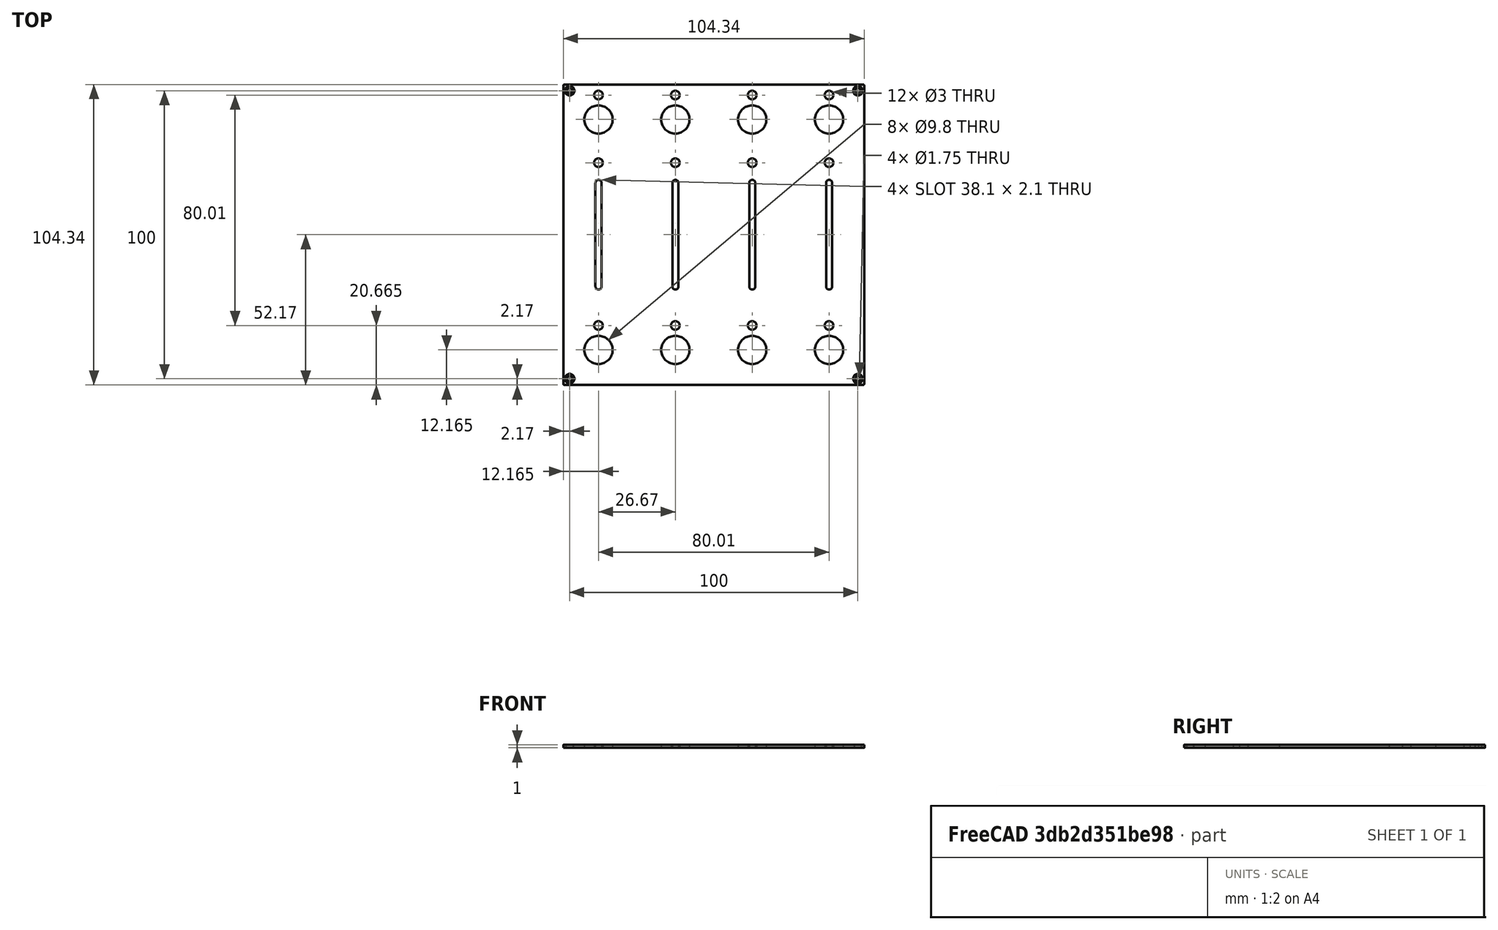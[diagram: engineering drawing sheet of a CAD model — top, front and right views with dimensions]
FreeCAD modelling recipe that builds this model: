
FCSTD DOCUMENT  (FreeCAD 0.21R33668 +26 (Git))
Label: FRONTPANEL-SHEET-PBF4
License: All rights reserved
LicenseURL: https://en.wikipedia.org/wiki/All_rights_reserved
objects: TechDraw::DrawViewBalloon×16, Sketcher::SketchObject×10, TechDraw::DrawViewDimension×9, PartDesign::Hole×6, TechDraw::DrawHatch×6, TechDraw::DrawViewPart×5, TechDraw::DrawViewAnnotation×3, TechDraw::DrawSVGTemplate×2, PartDesign::Pocket×2, PartDesign::Body×2, TechDraw::DrawPage×2, Spreadsheet::Sheet×1, PartDesign::Pad×1, PartDesign::FeatureBase×1, TechDraw::DrawComplexSection×1
note: 43 computed .brp shape members not serialized (recipe doc carries the construction recipe); baked Part::Feature solids carry a one-line shape summary decoded from their .brp

FEATURE [TechDraw::DrawSVGTemplate] Template
  EditableTexts = COLOR=Anodized matte black - RAL code: 9004; CreationDate=2024/05/14; E.G.APPROVED=APPROVED; FC-Scale=1:1; FC-Title=PBF4 - frontpanel; IntechStudioLtd.=Intech Studio Ltd.; MATERIAL=Aluminum 5052-H32; REV=04; STANDARD=ISO 2768 - m
  Height = 297
  Orientation = 1
  Template = <userpath>/Desktop/A3_LandscapeTD_MODIFIED.svg
  Width = 420
FEATURE [Spreadsheet::Sheet] Spreadsheet  label="dim"
  cells = A1='panel_length; B1(panel_length)=104.35; A2='panel_thickness; B2(panel_thickness)=1; A3='panel_radius; B3(panel_radius)==(104.35 - 103.6) / 2; A5='corner_drill_dist; B5(corner_drill_dist)=100; A6='corner_drill_dia; B6(corner_drill_dia)=1.75; A7='corner_drill_countersink; B7(corner_drill_countersink)=3.3; A9='undercut_width; B9(undercut_width)=1; A10='undercut_length; B10(undercut_length)=90; A11='undercut_offset; B11(undercut_offset)=1; A12='undercut_depth; B12(undercut_depth)=0.8; A14='ui_raster; B14(ui_raster)=26.67; A16='light_drill_dia; B16(light_drill_dia)=3; D16='old 2.9; A17='light_bore_dia; B17(light_bore_dia)=3.45; C17='check; D17='old 3.30; E17='DEPRICATED; A18='light_bore_depth; B18(light_bore_depth)=0.4; C18='check; D18='old 0.40; E18='DEPRICATED; A20='pot_drill_dia; B20(pot_drill_dia)=9.8; C20='check; D20='old 6.20; A21='pot_led_dist; B21(pot_led_dist)=8.5; B22=0; A23='but_drill_dia; B23(but_drill_dia)=9.8; A24='but_led_dist; B24(but_led_dist)=8.5; A26='fad_cutout_width; B26(fad_cutout_width)=2.1; C26='check; D26='old 1.50; A27='fad_cutout_length; B27(fad_cutout_length)=36; A28='fad_led_dist; B28(fad_led_dist)=25; A30='enc_drill_dia; B30(enc_drill_dia)=9.8; C30='check; D30='old 6.20; A31='enc_led_dist; B31(enc_led_dist)=8.5; A33='longfad_cutout_width; B33(longfad_cutout_width)=2.1; A34='longfad_cutout_length; B34(longfad_cutout_length)=66; A36='panel_chamfer; B36(panel_chamfer)=0.2; C36='UPDATE DRAWING
FEATURE [Sketcher::SketchObject] Sketch012
  FullyConstrained = true
  MapMode = 5
  Support = -> [XY_Plane003]
  expr: Constraints[21] = <<dim>>.fad_led_dist
  expr: Constraints[4] = <<dim>>.ui_raster
  sketch-geometry (9):
    g0: Circle CenterX=-40.005 CenterY=25 CenterZ=0 NormalX=0 NormalY=0 NormalZ=1 AngleXU=0 Radius=2
    g1: Circle CenterX=-13.335 CenterY=25 CenterZ=0 NormalX=0 NormalY=0 NormalZ=1 AngleXU=0 Radius=2
    g2: LineSegment StartX=-40.005 StartY=25 StartZ=0 EndX=-13.335 EndY=25 EndZ=0
    g3: Circle CenterX=13.335 CenterY=25 CenterZ=0 NormalX=0 NormalY=0 NormalZ=1 AngleXU=0 Radius=2
    g4: LineSegment StartX=-13.335 StartY=25 StartZ=0 EndX=13.335 EndY=25 EndZ=0
    g5: Circle CenterX=40.005 CenterY=25 CenterZ=0 NormalX=0 NormalY=0 NormalZ=1 AngleXU=0 Radius=2
    g6: LineSegment StartX=13.335 StartY=25 StartZ=0 EndX=40.005 EndY=25 EndZ=0
    g7: LineSegment StartX=-13.335 StartY=25 StartZ=0 EndX=0 EndY=0 EndZ=0
    g8: LineSegment StartX=0 StartY=0 StartZ=0 EndX=13.335 EndY=25 EndZ=0
  constraints (22):
    c: Diameter(g0) = 4
    c: Diameter(g1) = 4
    c: Coincident(g0,g2)
    c: Coincident(g1,g2)
    c: Distance(g2) = 26.67
    c: Angle(g2) = 0
    c: Diameter(g3) = 4
    c: Coincident(g1,g4)
    c: Coincident(g3,g4)
    c: Equal(g2,g4)
    c: Parallel(g4,g2)
    c: Diameter(g5) = 4
    c: Coincident(g3,g6)
    c: Coincident(g5,g6)
    c: Equal(g2,g6)
    c: Parallel(g6,g2)
    c: Coincident(g7,g1)
    c: Coincident(g7,g-1)
    c: Coincident(g7,g8)
    c: Coincident(g8,g3)
    c: Equal(g8,g7)
    c: DistanceY(g-1,g0) = 25
FEATURE [Sketcher::SketchObject] Sketch011
  FullyConstrained = true
  MapMode = 5
  Support = -> [XY_Plane003]
  expr: Constraints[17] = <<dim>>.ui_raster
  expr: Constraints[6] = <<dim>>.fad_cutout_width
  expr: Constraints[7] = <<dim>>.fad_cutout_length
  sketch-geometry (22):
    g0: ArcOfCircle CenterX=-40.005 CenterY=18 CenterZ=0 NormalX=0 NormalY=0 NormalZ=1 AngleXU=0 Radius=1.05 StartAngle=-1.26832e-11 EndAngle=3.14159
    g1: ArcOfCircle CenterX=-40.005 CenterY=-18 CenterZ=0 NormalX=0 NormalY=0 NormalZ=1 AngleXU=0 Radius=1.05 StartAngle=3.14159 EndAngle=6.28319
    g2: LineSegment StartX=-41.055 StartY=18 StartZ=0 EndX=-41.055 EndY=-18 EndZ=0
    g3: LineSegment StartX=-38.955 StartY=18 StartZ=0 EndX=-38.955 EndY=-18 EndZ=0
    g4: ArcOfCircle CenterX=-13.335 CenterY=18 CenterZ=0 NormalX=0 NormalY=0 NormalZ=1 AngleXU=0 Radius=1.05 StartAngle=2e-16 EndAngle=3.14159
    g5: ArcOfCircle CenterX=-13.335 CenterY=-18 CenterZ=0 NormalX=0 NormalY=0 NormalZ=1 AngleXU=0 Radius=1.05 StartAngle=3.14159 EndAngle=6.28319
    g6: LineSegment StartX=-14.385 StartY=18 StartZ=0 EndX=-14.385 EndY=-18 EndZ=0
    g7: LineSegment StartX=-12.285 StartY=18 StartZ=0 EndX=-12.285 EndY=-18 EndZ=0
    g8: LineSegment StartX=-38.955 StartY=18 StartZ=0 EndX=-12.285 EndY=18 EndZ=0
    g9: ArcOfCircle CenterX=13.335 CenterY=18 CenterZ=0 NormalX=0 NormalY=0 NormalZ=1 AngleXU=0 Radius=1.05 StartAngle=1.1e-15 EndAngle=3.14159
    g10: ArcOfCircle CenterX=13.335 CenterY=-18 CenterZ=0 NormalX=0 NormalY=0 NormalZ=1 AngleXU=0 Radius=1.05 StartAngle=3.14159 EndAngle=6.28319
    g11: LineSegment StartX=12.285 StartY=18 StartZ=0 EndX=12.285 EndY=-18 EndZ=0
    g12: LineSegment StartX=14.385 StartY=18 StartZ=0 EndX=14.385 EndY=-18 EndZ=0
    g13: LineSegment StartX=-12.285 StartY=18 StartZ=0 EndX=14.385 EndY=18 EndZ=0
    g14: ArcOfCircle CenterX=40.005 CenterY=18 CenterZ=0 NormalX=0 NormalY=0 NormalZ=1 AngleXU=0 Radius=1.05 StartAngle=9e-16 EndAngle=3.14159
    g15: ArcOfCircle CenterX=40.005 CenterY=-18 CenterZ=0 NormalX=0 NormalY=0 NormalZ=1 AngleXU=0 Radius=1.05 StartAngle=3.14159 EndAngle=6.28319
    g16: LineSegment StartX=38.955 StartY=18 StartZ=0 EndX=38.955 EndY=-18 EndZ=0
    g17: LineSegment StartX=41.055 StartY=18 StartZ=0 EndX=41.055 EndY=-18 EndZ=0
    g18: LineSegment StartX=14.385 StartY=18 StartZ=0 EndX=41.055 EndY=18 EndZ=0
    g19: LineSegment StartX=-13.335 StartY=18 StartZ=0 EndX=0 EndY=0 EndZ=0
    g20: LineSegment StartX=0 StartY=0 StartZ=0 EndX=13.335 EndY=18 EndZ=0
    g21: LineSegment StartX=0 StartY=0 StartZ=0 EndX=-13.335 EndY=-18 EndZ=0
  constraints (52):
    c: Tangent(g0,g3) = 1.5708
    c: Tangent(g0,g2) = -1.5708
    c: Tangent(g2,g1) = -1.5708
    c: Tangent(g3,g1) = 1.5708
    c: Vertical(g2)
    c: Equal(g0,g1)
    c: DistanceX(g0,g0) = 2.1
    c: DistanceY(g1,g0) = 36
    c: Tangent(g4,g7) = 1.5708
    c: Tangent(g4,g6) = -1.5708
    c: Tangent(g6,g5) = -1.5708
    c: Tangent(g7,g5) = 1.5708
    c: Vertical(g6)
    c: Equal(g4,g5)
    c: DistanceY(g5,g4) = 36
    c: Coincident(g0,g8)
    c: Coincident(g4,g8)
    c: Distance(g8) = 26.67
    c: Angle(g8) = 0
    c: Tangent(g9,g12) = 1.5708
    c: Tangent(g9,g11) = -1.5708
    c: Tangent(g11,g10) = -1.5708
    c: Tangent(g12,g10) = 1.5708
    c: Vertical(g11)
    c: Equal(g9,g10)
    c: DistanceY(g10,g9) = 36
    c: Coincident(g4,g13)
    c: Coincident(g9,g13)
    c: Equal(g8,g13)
    c: Parallel(g13,g8)
    c: Tangent(g14,g17) = 1.5708
    c: Tangent(g14,g16) = -1.5708
    c: Tangent(g16,g15) = -1.5708
    c: Tangent(g17,g15) = 1.5708
    c: Vertical(g16)
    c: Equal(g14,g15)
    c: DistanceY(g15,g14) = 36
    c: Coincident(g9,g18)
    c: Coincident(g14,g18)
    c: Equal(g8,g18)
    c: Parallel(g18,g8)
    c: Coincident(g19,g4)
    c: Coincident(g19,g-1)
    c: Coincident(g19,g20)
    c: Coincident(g20,g9)
    c: Coincident(g-1,g21)
    c: Coincident(g21,g5)
    c: Equal(g21,g19)
    c: Equal(g19,g20)
    c: Equal(g4,g9)
    c: Equal(g9,g14)
    c: Equal(g14,g0)
FEATURE [Sketcher::SketchObject] Sketch010
  FullyConstrained = true
  MapMode = 5
  Support = -> [XY_Plane003]
  expr: Constraints[20] = <<dim>>.ui_raster * 1.5
  expr: Constraints[21] = <<dim>>.pot_led_dist
  expr: Constraints[4] = <<dim>>.ui_raster
  sketch-geometry (9):
    g0: Circle CenterX=-40.005 CenterY=48.505 CenterZ=0 NormalX=0 NormalY=0 NormalZ=1 AngleXU=0 Radius=2
    g1: Circle CenterX=-13.335 CenterY=48.505 CenterZ=0 NormalX=0 NormalY=0 NormalZ=1 AngleXU=0 Radius=2
    g2: LineSegment StartX=-40.005 StartY=48.505 StartZ=0 EndX=-13.335 EndY=48.505 EndZ=0
    g3: Circle CenterX=13.335 CenterY=48.505 CenterZ=0 NormalX=0 NormalY=0 NormalZ=1 AngleXU=0 Radius=2
    g4: LineSegment StartX=-13.335 StartY=48.505 StartZ=0 EndX=13.335 EndY=48.505 EndZ=0
    g5: Circle CenterX=40.005 CenterY=48.505 CenterZ=0 NormalX=0 NormalY=0 NormalZ=1 AngleXU=0 Radius=2
    g6: LineSegment StartX=13.335 StartY=48.505 StartZ=0 EndX=40.005 EndY=48.505 EndZ=0
    g7: LineSegment StartX=-13.335 StartY=48.505 StartZ=0 EndX=0 EndY=40.005 EndZ=0
    g8: LineSegment StartX=0 StartY=40.005 StartZ=0 EndX=13.335 EndY=48.505 EndZ=0
  constraints (23):
    c: Diameter(g0) = 4
    c: Diameter(g1) = 4
    c: Coincident(g0,g2)
    c: Coincident(g1,g2)
    c: Distance(g2) = 26.67
    c: Angle(g2) = 0
    c: Diameter(g3) = 4
    c: Coincident(g1,g4)
    c: Coincident(g3,g4)
    c: Equal(g2,g4)
    c: Parallel(g4,g2)
    c: Diameter(g5) = 4
    c: Coincident(g3,g6)
    c: Coincident(g5,g6)
    c: Equal(g2,g6)
    c: Parallel(g6,g2)
    c: Coincident(g7,g1)
    c: PointOnObject(g7,g-2)
    c: Coincident(g7,g8)
    c: Coincident(g8,g3)
    c: DistanceY(g-1,g7) = 40.005
    c: DistanceY(g7,g1) = 8.5
    c: Equal(g8,g7)
FEATURE [Sketcher::SketchObject] Sketch009
  FullyConstrained = true
  MapMode = 5
  Support = -> [XY_Plane003]
  expr: Constraints[21] = <<dim>>.ui_raster * 1.5
  expr: Constraints[4] = <<dim>>.ui_raster
  sketch-geometry (9):
    g0: Circle CenterX=-40.005 CenterY=40.005 CenterZ=0 NormalX=0 NormalY=0 NormalZ=1 AngleXU=0 Radius=2
    g1: Circle CenterX=-13.335 CenterY=40.005 CenterZ=0 NormalX=0 NormalY=0 NormalZ=1 AngleXU=0 Radius=2
    g2: LineSegment StartX=-40.005 StartY=40.005 StartZ=0 EndX=-13.335 EndY=40.005 EndZ=0
    g3: Circle CenterX=13.335 CenterY=40.005 CenterZ=0 NormalX=0 NormalY=0 NormalZ=1 AngleXU=0 Radius=2
    g4: LineSegment StartX=-13.335 StartY=40.005 StartZ=0 EndX=13.335 EndY=40.005 EndZ=0
    g5: Circle CenterX=40.005 CenterY=40.005 CenterZ=0 NormalX=0 NormalY=0 NormalZ=1 AngleXU=0 Radius=2
    g6: LineSegment StartX=13.335 StartY=40.005 StartZ=0 EndX=40.005 EndY=40.005 EndZ=0
    g7: LineSegment StartX=-13.335 StartY=40.005 StartZ=0 EndX=0 EndY=0 EndZ=0
    g8: LineSegment StartX=0 StartY=0 StartZ=0 EndX=13.335 EndY=40.005 EndZ=0
  constraints (22):
    c: Diameter(g0) = 4
    c: Diameter(g1) = 4
    c: Coincident(g0,g2)
    c: Coincident(g1,g2)
    c: Distance(g2) = 26.67
    c: Angle(g2) = 0
    c: Diameter(g3) = 4
    c: Coincident(g1,g4)
    c: Coincident(g3,g4)
    c: Equal(g2,g4)
    c: Parallel(g4,g2)
    c: Diameter(g5) = 4
    c: Coincident(g3,g6)
    c: Coincident(g5,g6)
    c: Equal(g2,g6)
    c: Parallel(g6,g2)
    c: Coincident(g7,g1)
    c: Coincident(g7,g-1)
    c: Coincident(g7,g8)
    c: Coincident(g8,g3)
    c: Equal(g7,g8)
    c: DistanceY(g-1,g0) = 40.005
FEATURE [Sketcher::SketchObject] Sketch008
  FullyConstrained = true
  MapMode = 5
  Support = -> [XY_Plane003]
  expr: Constraints[21] = <<dim>>.ui_raster * 1.5
  expr: Constraints[22] = <<dim>>.but_led_dist
  expr: Constraints[4] = <<dim>>.ui_raster
  sketch-geometry (9):
    g0: Circle CenterX=-40.005 CenterY=-31.505 CenterZ=0 NormalX=0 NormalY=0 NormalZ=1 AngleXU=0 Radius=2
    g1: Circle CenterX=-13.335 CenterY=-31.505 CenterZ=0 NormalX=0 NormalY=0 NormalZ=1 AngleXU=0 Radius=2
    g2: LineSegment StartX=-40.005 StartY=-31.505 StartZ=0 EndX=-13.335 EndY=-31.505 EndZ=0
    g3: Circle CenterX=13.335 CenterY=-31.505 CenterZ=0 NormalX=0 NormalY=0 NormalZ=1 AngleXU=0 Radius=2
    g4: LineSegment StartX=-13.335 StartY=-31.505 StartZ=0 EndX=13.335 EndY=-31.505 EndZ=0
    g5: Circle CenterX=40.005 CenterY=-31.505 CenterZ=0 NormalX=0 NormalY=0 NormalZ=1 AngleXU=0 Radius=2
    g6: LineSegment StartX=13.335 StartY=-31.505 StartZ=0 EndX=40.005 EndY=-31.505 EndZ=0
    g7: LineSegment StartX=-13.335 StartY=-31.505 StartZ=0 EndX=0 EndY=-40.005 EndZ=0
    g8: LineSegment StartX=0 StartY=-40.005 StartZ=0 EndX=13.335 EndY=-31.505 EndZ=0
  constraints (23):
    c: Diameter(g0) = 4
    c: Diameter(g1) = 4
    c: Coincident(g0,g2)
    c: Coincident(g1,g2)
    c: Distance(g2) = 26.67
    c: Angle(g2) = 0
    c: Diameter(g3) = 4
    c: Coincident(g1,g4)
    c: Coincident(g3,g4)
    c: Equal(g2,g4)
    c: Parallel(g4,g2)
    c: Diameter(g5) = 4
    c: Coincident(g3,g6)
    c: Coincident(g5,g6)
    c: Equal(g2,g6)
    c: Parallel(g6,g2)
    c: Coincident(g7,g1)
    c: PointOnObject(g7,g-2)
    c: Coincident(g8,g7)
    c: Coincident(g8,g3)
    c: Equal(g8,g7)
    c: DistanceY(g7,g-1) = 40.005
    c: DistanceY(g7,g0) = 8.5
FEATURE [Sketcher::SketchObject] Sketch007
  FullyConstrained = true
  MapMode = 5
  Support = -> [XY_Plane003]
  expr: Constraints[16] = <<dim>>.ui_raster * 1.5
  expr: Constraints[4] = <<dim>>.ui_raster
  sketch-geometry (9):
    g0: Circle CenterX=-40.005 CenterY=-40.005 CenterZ=0 NormalX=0 NormalY=0 NormalZ=1 AngleXU=0 Radius=2
    g1: Circle CenterX=-13.335 CenterY=-40.005 CenterZ=0 NormalX=0 NormalY=0 NormalZ=1 AngleXU=0 Radius=2
    g2: LineSegment StartX=-40.005 StartY=-40.005 StartZ=0 EndX=-13.335 EndY=-40.005 EndZ=0
    g3: Circle CenterX=13.335 CenterY=-40.005 CenterZ=0 NormalX=0 NormalY=0 NormalZ=1 AngleXU=0 Radius=2
    g4: LineSegment StartX=-13.335 StartY=-40.005 StartZ=0 EndX=13.335 EndY=-40.005 EndZ=0
    g5: Circle CenterX=40.005 CenterY=-40.005 CenterZ=0 NormalX=0 NormalY=0 NormalZ=1 AngleXU=0 Radius=2
    g6: LineSegment StartX=13.335 StartY=-40.005 StartZ=0 EndX=40.005 EndY=-40.005 EndZ=0
    g7: LineSegment StartX=-13.335 StartY=-40.005 StartZ=0 EndX=0 EndY=0 EndZ=0
    g8: LineSegment StartX=0 StartY=0 StartZ=0 EndX=13.335 EndY=-40.005 EndZ=0
  constraints (22):
    c: Diameter(g0) = 4
    c: Diameter(g1) = 4
    c: Coincident(g0,g2)
    c: Coincident(g1,g2)
    c: Distance(g2) = 26.67
    c: Angle(g2) = 0
    c: Diameter(g3) = 4
    c: Coincident(g1,g4)
    c: Coincident(g3,g4)
    c: Equal(g2,g4)
    c: Parallel(g4,g2)
    c: Diameter(g5) = 4
    c: Coincident(g3,g6)
    c: Coincident(g5,g6)
    c: Equal(g2,g6)
    c: Parallel(g6,g2)
    c: DistanceY(g0,g-1) = 40.005
    c: Coincident(g7,g1)
    c: Coincident(g7,g-1)
    c: Coincident(g7,g8)
    c: Coincident(g8,g3)
    c: Equal(g8,g7)
FEATURE [Sketcher::SketchObject] Sketch001
  FullyConstrained = true
  MapMode = 5
  Support = -> [XY_Plane]
  expr: Constraints[13] = <<dim>>.corner_drill_dist
  sketch-geometry (9):
    g0: LineSegment StartX=-50 StartY=50 StartZ=0 EndX=-50 EndY=-50 EndZ=0
    g1: LineSegment StartX=-50 StartY=-50 StartZ=0 EndX=50 EndY=-50 EndZ=0
    g2: LineSegment StartX=50 StartY=-50 StartZ=0 EndX=50 EndY=50 EndZ=0
    g3: LineSegment StartX=50 StartY=50 StartZ=0 EndX=-50 EndY=50 EndZ=0
    g4: Circle CenterX=0 CenterY=0 CenterZ=0 NormalX=0 NormalY=0 NormalZ=1 AngleXU=0 Radius=70.7107
    g5: Circle CenterX=-50 CenterY=50 CenterZ=0 NormalX=0 NormalY=0 NormalZ=1 AngleXU=0 Radius=0.5
    g6: Circle CenterX=50 CenterY=50 CenterZ=0 NormalX=0 NormalY=0 NormalZ=1 AngleXU=0 Radius=0.5
    g7: Circle CenterX=50 CenterY=-50 CenterZ=0 NormalX=0 NormalY=0 NormalZ=1 AngleXU=0 Radius=0.5
    g8: Circle CenterX=-50 CenterY=-50 CenterZ=0 NormalX=0 NormalY=0 NormalZ=1 AngleXU=0 Radius=0.5
  constraints (22):
    c: Coincident(g0,g1)
    c: Coincident(g1,g2)
    c: Coincident(g2,g3)
    c: Coincident(g3,g0)
    c: Equal(g0,g1)
    c: Equal(g0,g2)
    c: Equal(g0,g3)
    c: PointOnObject(g0,g4)
    c: PointOnObject(g1,g4)
    c: PointOnObject(g2,g4)
    c: PointOnObject(g3,g4)
    c: Coincident(g4,g-1)
    c: Horizontal(g3)
    c: DistanceX(g3,g3) = 100
    c: Coincident(g5,g0)
    c: Coincident(g6,g2)
    c: Coincident(g7,g1)
    c: Coincident(g8,g0)
    c: Diameter(g8) = 1
    c: Equal(g8,g7)
    c: Equal(g8,g6)
    c: Equal(g8,g5)
FEATURE [Sketcher::SketchObject] Sketch002
  AttachmentOffset = pos=(0,0,-4.8) rot=(0,0,1;0rad)
  FullyConstrained = true
  MapMode = 5
  Placement = pos=(0,0,-4.8) rot=(0,0,1;0rad)
  Support = -> [XY_Plane]
  expr: .AttachmentOffset.Base.z = -<<dim>>.undercut_depth - 4
  expr: Constraints[91] = <<dim>>.undercut_length
  expr: Constraints[92] = <<dim>>.undercut_width
  expr: Constraints[93] = <<dim>>.panel_length / 2 - <<dim>>.undercut_offset - <<dim>>.undercut_width / 2
  sketch-geometry (40):
    g0: LineSegment StartX=-45 StartY=50.175 StartZ=0 EndX=45 EndY=50.175 EndZ=0
    g1: LineSegment StartX=-45 StartY=51.175 StartZ=0 EndX=45 EndY=51.175 EndZ=0
    g2: LineSegment StartX=-50.675 StartY=45 StartZ=0 EndX=0 EndY=0 EndZ=0
    g3: LineSegment StartX=0 StartY=0 StartZ=0 EndX=-50.675 EndY=-45 EndZ=0
    g4: LineSegment StartX=0 StartY=0 StartZ=0 EndX=-45 EndY=50.675 EndZ=0
    g5: LineSegment StartX=45 StartY=50.675 StartZ=0 EndX=0 EndY=0 EndZ=0
    g6: LineSegment StartX=0 StartY=0 StartZ=0 EndX=50.675 EndY=45 EndZ=0
    g7: LineSegment StartX=50.675 StartY=-45 StartZ=0 EndX=0 EndY=0 EndZ=0
    g8: LineSegment StartX=0 StartY=0 StartZ=0 EndX=45 EndY=-50.675 EndZ=0
    g9: LineSegment StartX=0 StartY=0 StartZ=0 EndX=-45 EndY=-50.675 EndZ=0
    g10: ArcOfCircle CenterX=45 CenterY=50.675 CenterZ=0 NormalX=0 NormalY=0 NormalZ=1 AngleXU=0 Radius=0.5 StartAngle=4.71239 EndAngle=6.28319
    g11: ArcOfCircle CenterX=45 CenterY=50.675 CenterZ=0 NormalX=0 NormalY=0 NormalZ=1 AngleXU=0 Radius=0.5 StartAngle=0 EndAngle=1.5708
    g12: LineSegment StartX=45 StartY=50.675 StartZ=0 EndX=45.5 EndY=50.675 EndZ=0
    g13: ArcOfCircle CenterX=-45 CenterY=50.675 CenterZ=0 NormalX=0 NormalY=0 NormalZ=1 AngleXU=0 Radius=0.5 StartAngle=3.14159 EndAngle=4.71239
    g14: ArcOfCircle CenterX=-45 CenterY=50.675 CenterZ=0 NormalX=0 NormalY=0 NormalZ=1 AngleXU=0 Radius=0.5 StartAngle=1.5708 EndAngle=3.14159
    g15: LineSegment StartX=-45.5 StartY=50.675 StartZ=0 EndX=-45 EndY=50.675 EndZ=0
    g16: LineSegment StartX=-45 StartY=-51.175 StartZ=0 EndX=45 EndY=-51.175 EndZ=0
    g17: LineSegment StartX=-45 StartY=-50.175 StartZ=0 EndX=45 EndY=-50.175 EndZ=0
    g18: ArcOfCircle CenterX=45 CenterY=-50.675 CenterZ=0 NormalX=0 NormalY=0 NormalZ=1 AngleXU=0 Radius=0.5 StartAngle=4.71239 EndAngle=6.28319
    g19: ArcOfCircle CenterX=45 CenterY=-50.675 CenterZ=0 NormalX=0 NormalY=0 NormalZ=1 AngleXU=0 Radius=0.5 StartAngle=0 EndAngle=1.5708
    g20: LineSegment StartX=45 StartY=-50.675 StartZ=0 EndX=45.5 EndY=-50.675 EndZ=0
    g21: ArcOfCircle CenterX=-45 CenterY=-50.675 CenterZ=0 NormalX=0 NormalY=0 NormalZ=1 AngleXU=0 Radius=0.5 StartAngle=3.14159 EndAngle=4.71239
    g22: ArcOfCircle CenterX=-45 CenterY=-50.675 CenterZ=0 NormalX=0 NormalY=0 NormalZ=1 AngleXU=0 Radius=0.5 StartAngle=1.5708 EndAngle=3.14159
    g23: LineSegment StartX=-45.5 StartY=-50.675 StartZ=0 EndX=-45 EndY=-50.675 EndZ=0
    g24: LineSegment StartX=51.175 StartY=-45 StartZ=0 EndX=51.175 EndY=45 EndZ=0
    g25: LineSegment StartX=50.175 StartY=-45 StartZ=0 EndX=50.175 EndY=45 EndZ=0
    g26: ArcOfCircle CenterX=50.675 CenterY=45 CenterZ=0 NormalX=0 NormalY=0 NormalZ=1 AngleXU=0 Radius=0.5 StartAngle=3.8e-15 EndAngle=1.5708
    g27: ArcOfCircle CenterX=50.675 CenterY=45 CenterZ=0 NormalX=0 NormalY=0 NormalZ=1 AngleXU=0 Radius=0.5 StartAngle=1.5708 EndAngle=3.14159
    g28: LineSegment StartX=50.675 StartY=45 StartZ=0 EndX=50.675 EndY=45.5 EndZ=0
    g29: ArcOfCircle CenterX=50.675 CenterY=-45 CenterZ=0 NormalX=0 NormalY=0 NormalZ=1 AngleXU=0 Radius=0.5 StartAngle=4.71239 EndAngle=6.28319
    g30: ArcOfCircle CenterX=50.675 CenterY=-45 CenterZ=0 NormalX=0 NormalY=0 NormalZ=1 AngleXU=0 Radius=0.5 StartAngle=3.14159 EndAngle=4.71239
    g31: LineSegment StartX=50.675 StartY=-45.5 StartZ=0 EndX=50.675 EndY=-45 EndZ=0
    g32: LineSegment StartX=-50.175 StartY=-45 StartZ=0 EndX=-50.175 EndY=45 EndZ=0
    g33: LineSegment StartX=-51.175 StartY=-45 StartZ=0 EndX=-51.175 EndY=45 EndZ=0
    g34: ArcOfCircle CenterX=-50.675 CenterY=45 CenterZ=0 NormalX=0 NormalY=0 NormalZ=1 AngleXU=0 Radius=0.5 StartAngle=1.4e-15 EndAngle=1.5708
    g35: ArcOfCircle CenterX=-50.675 CenterY=45 CenterZ=0 NormalX=0 NormalY=0 NormalZ=1 AngleXU=0 Radius=0.5 StartAngle=1.5708 EndAngle=3.14159
    g36: LineSegment StartX=-50.675 StartY=45 StartZ=0 EndX=-50.675 EndY=45.5 EndZ=0
    g37: ArcOfCircle CenterX=-50.675 CenterY=-45 CenterZ=0 NormalX=0 NormalY=0 NormalZ=1 AngleXU=0 Radius=0.5 StartAngle=4.71239 EndAngle=6.28319
    g38: ArcOfCircle CenterX=-50.675 CenterY=-45 CenterZ=0 NormalX=0 NormalY=0 NormalZ=1 AngleXU=0 Radius=0.5 StartAngle=3.14159 EndAngle=4.71239
    g39: LineSegment StartX=-50.675 StartY=-45.5 StartZ=0 EndX=-50.675 EndY=-45 EndZ=0
  constraints (96):
    c: Horizontal(g0)
    c: Coincident(g2,g-1)
    c: Coincident(g2,g3)
    c: Coincident(g-1,g4)
    c: Coincident(g5,g-1)
    c: Coincident(g5,g6)
    c: Coincident(g7,g-1)
    c: Coincident(g7,g8)
    c: Coincident(g-1,g9)
    c: Equal(g5,g6)
    c: Equal(g6,g8)
    c: Equal(g8,g7)
    c: Equal(g7,g9)
    c: Equal(g9,g3)
    c: Equal(g3,g2)
    c: Equal(g2,g4)
    c: Coincident(g10,g5)
    c: Coincident(g11,g10)
    c: Coincident(g11,g10)
    c: Tangent(g11,g1) = 1.5708
    c: Tangent(g10,g0) = -1.5708
    c: Coincident(g12,g10)
    c: Coincident(g12,g10)
    c: Horizontal(g12)
    c: Coincident(g13,g4)
    c: Coincident(g14,g13)
    c: Coincident(g14,g13)
    c: Tangent(g14,g1) = 1.5708
    c: Tangent(g13,g0) = -1.5708
    c: Coincident(g15,g13)
    c: Coincident(g15,g13)
    c: Horizontal(g15)
    c: Horizontal(g1)
    c: Horizontal(g16)
    c: Coincident(g19,g18)
    c: Coincident(g19,g18)
    c: Tangent(g19,g17) = 1.5708
    c: Tangent(g18,g16) = -1.5708
    c: Coincident(g20,g18)
    c: Coincident(g20,g18)
    c: Horizontal(g20)
    c: Coincident(g22,g21)
    c: Coincident(g22,g21)
    c: Tangent(g22,g17) = 1.5708
    c: Tangent(g21,g16) = -1.5708
    c: Coincident(g23,g21)
    c: Coincident(g23,g21)
    c: Horizontal(g23)
    c: Horizontal(g17)
    c: Coincident(g21,g9)
    c: Coincident(g8,g18)
    c: Equal(g22,g14)
    c: Equal(g17,g1)
    c: Coincident(g27,g26)
    c: Coincident(g27,g26)
    c: Tangent(g27,g25) = 1.5708
    c: Tangent(g26,g24) = -1.5708
    c: Coincident(g28,g26)
    c: Coincident(g28,g26)
    c: Coincident(g30,g29)
    c: Coincident(g30,g29)
    c: Tangent(g30,g25) = 1.5708
    c: Tangent(g29,g24) = -1.5708
    c: Coincident(g31,g29)
    c: Coincident(g31,g29)
    c: Vertical(g31)
    c: Vertical(g28)
    c: Vertical(g25)
    c: Vertical(g24)
    c: Coincident(g35,g34)
    c: Coincident(g35,g34)
    c: Tangent(g35,g33) = 1.5708
    c: Tangent(g34,g32) = -1.5708
    c: Coincident(g36,g34)
    c: Coincident(g36,g34)
    c: Coincident(g38,g37)
    c: Coincident(g38,g37)
    c: Tangent(g38,g33) = 1.5708
    c: Tangent(g37,g32) = -1.5708
    c: Coincident(g39,g37)
    c: Coincident(g39,g37)
    c: Vertical(g39)
    c: Vertical(g36)
    c: Vertical(g33)
    c: Vertical(g32)
    c: Coincident(g6,g26)
    c: Coincident(g7,g29)
    c: Equal(g25,g0)
    c: Equal(g11,g27)
    c: Equal(g1,g33)
    c: Equal(g35,g11)
    c: DistanceX(g13,g10) = 90
    c: Diameter(g13) = 1
    c: DistanceY(g-1,g13) = 50.675
    c: Coincident(g2,g34)
    c: Coincident(g3,g37)
FEATURE [Sketcher::SketchObject] Sketch
  FullyConstrained = true
  MapMode = 5
  Support = -> [XY_Plane]
  expr: Constraints[12] = <<dim>>.panel_radius
  expr: Constraints[16] = <<dim>>.panel_length
  sketch-geometry (11):
    g0: LineSegment StartX=-51.8 StartY=52.175 StartZ=0 EndX=51.8 EndY=52.175 EndZ=0
    g1: LineSegment StartX=52.175 StartY=51.8 StartZ=0 EndX=52.175 EndY=-51.8 EndZ=0
    g2: LineSegment StartX=51.8 StartY=-52.175 StartZ=0 EndX=-51.8 EndY=-52.175 EndZ=0
    g3: LineSegment StartX=-52.175 StartY=-51.8 StartZ=0 EndX=-52.175 EndY=51.8 EndZ=0
    g4: ArcOfCircle CenterX=-51.8 CenterY=51.8 CenterZ=0 NormalX=0 NormalY=0 NormalZ=1 AngleXU=0 Radius=0.375 StartAngle=1.5708 EndAngle=3.14159
    g5: ArcOfCircle CenterX=51.8 CenterY=51.8 CenterZ=0 NormalX=0 NormalY=0 NormalZ=1 AngleXU=0 Radius=0.375 StartAngle=8.4e-15 EndAngle=1.5708
    g6: ArcOfCircle CenterX=51.8 CenterY=-51.8 CenterZ=0 NormalX=0 NormalY=0 NormalZ=1 AngleXU=0 Radius=0.375 StartAngle=4.71239 EndAngle=6.28319
    g7: ArcOfCircle CenterX=-51.8 CenterY=-51.8 CenterZ=0 NormalX=0 NormalY=0 NormalZ=1 AngleXU=0 Radius=0.375 StartAngle=3.14159 EndAngle=4.71239
    g8: LineSegment StartX=-51.8 StartY=51.8 StartZ=0 EndX=0 EndY=0 EndZ=0
    g9: LineSegment StartX=0 StartY=0 StartZ=0 EndX=51.8 EndY=51.8 EndZ=0
    g10: LineSegment StartX=0 StartY=0 StartZ=0 EndX=-51.8 EndY=-51.8 EndZ=0
  constraints (26):
    c: Horizontal(g0)
    c: Horizontal(g2)
    c: Vertical(g1)
    c: Vertical(g3)
    c: Tangent(g3,g4) = 1.5708
    c: Tangent(g0,g4) = 1.5708
    c: Tangent(g0,g5) = 1.5708
    c: Tangent(g1,g5) = 1.5708
    c: Tangent(g1,g6) = 1.5708
    c: Tangent(g2,g6) = 1.5708
    c: Tangent(g2,g7) = 1.5708
    c: Tangent(g3,g7) = 1.5708
    c: Radius(g4) = 0.375
    c: Equal(g4,g5)
    c: Equal(g4,g6)
    c: Equal(g4,g7)
    c: DistanceX(g3,g1) = 104.35
    c: Equal(g3,g0)
    c: Coincident(g8,g4)
    c: Coincident(g8,g-1)
    c: Coincident(g8,g9)
    c: Coincident(g9,g5)
    c: Coincident(g-1,g10)
    c: Coincident(g10,g7)
    c: Equal(g10,g8)
    c: Equal(g8,g9)
FEATURE [PartDesign::Pad] Pad  label="panel"
  AllowMultiFace = false
  Direction = (0,0,1)
  Length = 1
  Length2 = 100
  Profile = -> Sketch
  Reversed = true
  Type = 0
  expr: Length = <<dim>>.panel_thickness
FEATURE [PartDesign::Pocket] Pocket
  AllowMultiFace = false
  BaseFeature = -> Pad
  Direction = (0,0,-1)
  Length = 5
  Length2 = 100
  Profile = -> Sketch002
  Type = 1
FEATURE [PartDesign::Hole] Hole
  BaseFeature = -> Pocket
  CustomThreadClearance = 0
  Depth = 298.105
  DepthType = 1
  Diameter = 1.75
  DrillForDepth = false
  DrillPoint = 1
  DrillPointAngle = 118
  HoleCutCountersinkAngle = 90
  HoleCutCustomValues = false
  HoleCutDepth = 0
  HoleCutDiameter = 3.3
  HoleCutType = 2
  ModelThread = false
  Profile = -> Sketch001
  Tapered = false
  TaperedAngle = 90
  ThreadClass = 0
  ThreadDepth = 298.105
  ThreadDepthType = 0
  ThreadDirection = 0
  ThreadFit = 0
  ThreadSize = 0
  ThreadType = 0
  Threaded = false
  UseCustomThreadClearance = false
  expr: Diameter = <<dim>>.corner_drill_dia
  expr: HoleCutDiameter = <<dim>>.corner_drill_countersink
FEATURE [PartDesign::Body] Body  label="Base"
  Group = -> [Sketch,Pad,Sketch001,Sketch002,Pocket,Hole]
  Origin = -> Origin
  Tip = -> Hole
FEATURE [PartDesign::FeatureBase] Clone002
  BaseFeature = -> Body
FEATURE [PartDesign::Hole] Hole005  label="PBF4_ButtonHole"
  AllowMultiFace = false
  BaseFeature = -> Clone002
  CustomThreadClearance = 0
  Depth = 25
  DepthType = 1
  Diameter = 9.8
  DrillForDepth = false
  DrillPoint = 0
  DrillPointAngle = 118
  HoleCutCountersinkAngle = 90
  HoleCutCustomValues = false
  HoleCutDepth = 0
  HoleCutDiameter = 0
  HoleCutType = 0
  ModelThread = false
  Profile = -> Sketch007
  Tapered = false
  TaperedAngle = 90
  ThreadClass = 0
  ThreadDepth = 23.5
  ThreadDepthType = 0
  ThreadDirection = 0
  ThreadFit = 0
  ThreadSize = 0
  ThreadType = 0
  Threaded = false
  UseCustomThreadClearance = false
  expr: Diameter = <<dim>>.but_drill_dia
FEATURE [PartDesign::Hole] Hole006  label="PBF4_ButtonLight"
  AllowMultiFace = false
  BaseFeature = -> Hole005
  CustomThreadClearance = 0
  Depth = 25
  DepthType = 1
  Diameter = 3
  DrillForDepth = false
  DrillPoint = 0
  DrillPointAngle = 118
  HoleCutCountersinkAngle = 90
  HoleCutCustomValues = false
  HoleCutDepth = 0.4
  HoleCutDiameter = 3.45
  HoleCutType = 0
  ModelThread = false
  Profile = -> Sketch008
  Tapered = false
  TaperedAngle = 90
  ThreadClass = 0
  ThreadDepth = 23.5
  ThreadDepthType = 0
  ThreadDirection = 0
  ThreadFit = 0
  ThreadSize = 0
  ThreadType = 0
  Threaded = false
  UseCustomThreadClearance = false
  expr: Diameter = <<dim>>.light_drill_dia
  expr: HoleCutDepth = <<dim>>.light_bore_depth
  expr: HoleCutDiameter = <<dim>>.light_bore_dia
FEATURE [PartDesign::Hole] Hole007
  AllowMultiFace = false
  BaseFeature = -> Hole006
  CustomThreadClearance = 0
  Depth = 25
  DepthType = 1
  Diameter = 9.8
  DrillForDepth = false
  DrillPoint = 0
  DrillPointAngle = 118
  HoleCutCountersinkAngle = 90
  HoleCutCustomValues = false
  HoleCutDepth = 0
  HoleCutDiameter = 0
  HoleCutType = 0
  ModelThread = false
  Profile = -> Sketch009
  Tapered = false
  TaperedAngle = 90
  ThreadClass = 0
  ThreadDepth = 23.5
  ThreadDepthType = 0
  ThreadDirection = 0
  ThreadFit = 0
  ThreadSize = 0
  ThreadType = 0
  Threaded = false
  UseCustomThreadClearance = false
  expr: Diameter = <<dim>>.pot_drill_dia
FEATURE [PartDesign::Hole] Hole008
  AllowMultiFace = false
  BaseFeature = -> Hole007
  CustomThreadClearance = 0
  Depth = 25
  DepthType = 1
  Diameter = 3
  DrillForDepth = false
  DrillPoint = 1
  DrillPointAngle = 118
  HoleCutCountersinkAngle = 90
  HoleCutCustomValues = false
  HoleCutDepth = 0.4
  HoleCutDiameter = 3.45
  HoleCutType = 0
  ModelThread = false
  Profile = -> Sketch010
  Tapered = false
  TaperedAngle = 90
  ThreadClass = 0
  ThreadDepth = 23.5
  ThreadDepthType = 0
  ThreadDirection = 0
  ThreadFit = 0
  ThreadSize = 0
  ThreadType = 0
  Threaded = false
  UseCustomThreadClearance = false
  expr: Diameter = <<dim>>.light_drill_dia
  expr: HoleCutDepth = <<dim>>.light_bore_depth
  expr: HoleCutDiameter = <<dim>>.light_bore_dia
FEATURE [PartDesign::Pocket] Pocket001
  AllowMultiFace = false
  BaseFeature = -> Hole008
  Direction = (0,0,-1)
  Length = 5
  Length2 = 100
  Profile = -> Sketch011
  Type = 1
FEATURE [PartDesign::Hole] Hole009
  AllowMultiFace = false
  BaseFeature = -> Pocket001
  CustomThreadClearance = 0
  Depth = 25
  DepthType = 1
  Diameter = 3
  DrillForDepth = false
  DrillPoint = 0
  DrillPointAngle = 118
  HoleCutCountersinkAngle = 90
  HoleCutCustomValues = false
  HoleCutDepth = 0.4
  HoleCutDiameter = 3.45
  HoleCutType = 0
  ModelThread = false
  Profile = -> Sketch012
  Tapered = false
  TaperedAngle = 90
  ThreadClass = 0
  ThreadDepth = 23.5
  ThreadDepthType = 0
  ThreadDirection = 0
  ThreadFit = 0
  ThreadSize = 0
  ThreadType = 0
  Threaded = false
  UseCustomThreadClearance = false
  expr: Diameter = <<dim>>.light_drill_dia
  expr: HoleCutDepth = <<dim>>.light_bore_depth
  expr: HoleCutDiameter = <<dim>>.light_bore_dia
FEATURE [Sketcher::SketchObject] Sketch013
  ExternalGeometry = -> [Hole009]
  FullyConstrained = true
  MapMode = 5
  Support = -> [XY_Plane003]
  sketch-geometry (1):
    g0: LineSegment StartX=-53.5 StartY=-50 StartZ=0 EndX=-46.5 EndY=-50 EndZ=0
  constraints (3):
    c: Horizontal(g0)
    c: Symmetric(g0,g0,g-3)
    c: DistanceX(g0,g0) = 7
FEATURE [PartDesign::Body] Body003  label="FRONTPANEL-SHEET-PBF4"
  BaseFeature = -> Body
  Group = -> [Clone002,Sketch007,Hole005,Sketch008,Hole006,Sketch009,Hole007,Sketch010,Hole008,Sketch011,Pocket001,Sketch012,Hole009,Sketch013]
  Origin = -> Origin003
  Tip = -> Hole009
FEATURE [TechDraw::DrawViewPart] View004
  CoarseView = false
  Direction = (0,0,1)
  Focus = 100
  HardHidden = true
  IsoCount = 0
  IsoHidden = false
  IsoVisible = false
  LockPosition = false
  Perspective = false
  Rotation = 0
  ScaleType = 0
  ScrubCount = 0
  SeamHidden = false
  SeamVisible = true
  SmoothHidden = false
  SmoothVisible = true
  Source = -> [Body003]
  X = 89.7467
  XDirection = (1,0.000691,0)
  Y = 211.66
FEATURE [TechDraw::DrawViewPart] View005
  CoarseView = false
  Direction = (-1,-0.000691,0)
  Focus = 100
  HardHidden = true
  IsoCount = 0
  IsoHidden = false
  IsoVisible = false
  LockPosition = false
  Perspective = false
  Rotation = 0
  ScaleType = 0
  ScrubCount = 0
  SeamHidden = false
  SeamVisible = true
  SmoothHidden = false
  SmoothVisible = true
  Source = -> [Body003]
  X = 192.719
  XDirection = (0,0,1)
  Y = 213.296
FEATURE [TechDraw::DrawViewPart] View006
  CoarseView = false
  Direction = (0,0,-1)
  Focus = 100
  HardHidden = true
  IsoCount = 0
  IsoHidden = false
  IsoVisible = false
  LockPosition = false
  Perspective = false
  Rotation = 0
  ScaleType = 0
  ScrubCount = 0
  SeamHidden = false
  SeamVisible = true
  SmoothHidden = false
  SmoothVisible = true
  Source = -> [Body003]
  X = 288.25
  XDirection = (-1,-0.000691,0)
  Y = 206.566
FEATURE [TechDraw::DrawViewBalloon] Balloon021
  BubbleShape = 1
  EndType = 0
  EndTypeScale = 1
  KinkLength = 1
  LockPosition = false
  OriginX = -52.3988
  OriginY = 52.0113
  Rotation = 0
  ScaleType = 0
  ShapeScale = 1
  SourceView = -> View004
  Text = 4x R0,38
  TextWrapLen = -1
  X = -66.8562
  Y = 62.9967
FEATURE [TechDraw::DrawViewDimension] Dimension
  AngleOverride = false
  Arbitrary = false
  ArbitraryTolerances = true
  EqualTolerance = false
  ExtensionAngle = 0
  FormatSpec = 8x ⌀%.2w
  FormatSpecOverTolerance = +0,15
  FormatSpecUnderTolerance = 0
  Inverted = false
  LineAngle = 0
  LockPosition = false
  MeasureType = 1
  OverTolerance = 0
  References2D = -> [View004]
  Rotation = 0
  ScaleType = 0
  TheoreticalExact = false
  Type = 5
  UnderTolerance = 0
  X = -23.4377
  Y = -60.2217
FEATURE [TechDraw::DrawViewDimension] Dimension011
  AngleOverride = false
  Arbitrary = false
  ArbitraryTolerances = false
  EqualTolerance = true
  ExtensionAngle = 0
  FormatSpec = 12x ⌀%.2w
  FormatSpecOverTolerance = %+.2w
  FormatSpecUnderTolerance = %+.2w
  Inverted = false
  LineAngle = 0
  LockPosition = false
  MeasureType = 1
  OverTolerance = 0.05
  References2D = -> [View004]
  Rotation = 0
  ScaleType = 0
  TheoreticalExact = false
  Type = 5
  UnderTolerance = -0.05
  X = 75.2192
  Y = -60.9974
FEATURE [TechDraw::DrawViewBalloon] Balloon025
  BubbleShape = 6
  EndType = 6
  EndTypeScale = 1
  KinkLength = 0
  LockPosition = false
  OriginX = -33.2827
  OriginY = -76.0399
  Rotation = 0
  ScaleType = 0
  ShapeScale = 1
  SourceView = -> Dimension
  Text = ⌖|⌀ 0,15|A|B|C
  TextWrapLen = -1
  X = -3.66455
  Y = -72.8111
FEATURE [TechDraw::DrawViewBalloon] Balloon026
  BubbleShape = 6
  EndType = 6
  EndTypeScale = 1
  KinkLength = 0
  LockPosition = false
  OriginX = -27.702
  OriginY = -92.6195
  Rotation = 0
  ScaleType = 0
  ShapeScale = 1
  SourceView = -> Balloon025
  Text = ○|0,1
  TextWrapLen = -1
  X = -22.7116
  Y = -83.3046
FEATURE [TechDraw::DrawViewBalloon] Balloon027
  BubbleShape = 6
  EndType = 6
  EndTypeScale = 1
  KinkLength = 0
  LockPosition = false
  OriginX = 78.2436
  OriginY = -79.5754
  Rotation = 0
  ScaleType = 0
  ShapeScale = 1
  SourceView = -> Dimension011
  Text = ⌖|⌀0,15|A|B|C
  TextWrapLen = -1
  X = 87.0632
  Y = -71.8034
FEATURE [TechDraw::DrawComplexSection] ComplexSection  label="Section A - A"
  BaseView = -> View004
  Caption = Section A-A
  CoarseView = false
  CutSurfaceDisplay = 3
  CuttingToolWireObject = -> Sketch013
  Direction = (0.000691,-1,0)
  FileGeomPattern = C:/Program Files/FreeCAD 0.21/data/Mod/TechDraw/PAT/FCPAT.pat
  FileHatchPattern = C:/Program Files/FreeCAD 0.21/data/Mod/TechDraw/Patterns/simple.svg
  Focus = 100
  FuseBeforeCut = false
  HardHidden = true
  HatchOffset = (0,0,0)
  HatchRotation = 0
  HatchScale = 1
  IsoCount = 0
  IsoHidden = false
  IsoVisible = false
  LockPosition = false
  NameGeomPattern = Gyémánt bevonatú
  Perspective = false
  ProjectionStrategy = 1
  Rotation = 0
  Scale = 10
  ScaleType = 2
  ScrubCount = 0
  SeamHidden = false
  SeamVisible = true
  SectionDirection = 4
  SectionNormal = (0.000691,-1,0)
  SectionOrigin = (0,0,0)
  SectionSymbol = A
  SmoothHidden = false
  SmoothVisible = true
  Source = -> [Body003]
  TrimAfterCut = false
  X = 86.3912
  XDirection = (1,0.000691,0)
  Y = 73.924
FEATURE [TechDraw::DrawHatch] Hatch  label="HatchF1"
  HatchPattern = C:/Program Files/FreeCAD 0.21/data/Mod/TechDraw/Patterns/simple.svg
  Source = -> ComplexSection [Face1]
FEATURE [TechDraw::DrawHatch] Hatch001  label="Hatch001F3"
  HatchPattern = C:/Program Files/FreeCAD 0.21/data/Mod/TechDraw/Patterns/simple.svg
  Source = -> ComplexSection [Face3]
FEATURE [TechDraw::DrawViewDimension] Dimension012
  AngleOverride = false
  Arbitrary = false
  ArbitraryTolerances = false
  EqualTolerance = true
  ExtensionAngle = 0
  FormatSpec = (%.2w)
  FormatSpecOverTolerance = %+.2w
  FormatSpecUnderTolerance = %+.2w
  Inverted = false
  LineAngle = 0
  LockPosition = false
  MeasureType = 1
  OverTolerance = 0
  References2D = -> [ComplexSection]
  Rotation = 0
  ScaleType = 0
  TheoreticalExact = false
  Type = 2
  UnderTolerance = 0
  X = -41.335
  Y = 2.5
FEATURE [TechDraw::DrawViewDimension] Dimension013
  AngleOverride = false
  Arbitrary = false
  ArbitraryTolerances = false
  EqualTolerance = true
  ExtensionAngle = 0
  FormatSpec = 4x ⌀%.2w
  FormatSpecOverTolerance = %+.2w
  FormatSpecUnderTolerance = %+.2w
  Inverted = false
  LineAngle = 0
  LockPosition = false
  MeasureType = 1
  OverTolerance = 0
  References2D = -> [ComplexSection]
  Rotation = 0
  ScaleType = 0
  TheoreticalExact = false
  Type = 1
  UnderTolerance = 0
  X = 22.526
  Y = 21.5673
FEATURE [TechDraw::DrawViewDimension] Dimension014
  AngleOverride = false
  Arbitrary = false
  ArbitraryTolerances = false
  EqualTolerance = true
  ExtensionAngle = 0
  FormatSpec = %.2w
  FormatSpecOverTolerance = %+.2w
  FormatSpecUnderTolerance = %+.2w
  Inverted = false
  LineAngle = 0
  LockPosition = false
  MeasureType = 1
  OverTolerance = 0
  References2D = -> [ComplexSection]
  Rotation = 0
  ScaleType = 0
  TheoreticalExact = false
  Type = 6
  UnderTolerance = 0
  X = -27.7612
  Y = 28.1448
FEATURE [TechDraw::DrawViewDimension] Dimension015
  AngleOverride = false
  Arbitrary = false
  ArbitraryTolerances = false
  EqualTolerance = true
  ExtensionAngle = 0
  FormatSpec = 4x ⌀%.2w
  FormatSpecOverTolerance = %+.2w
  FormatSpecUnderTolerance = %+.2w
  Inverted = false
  LineAngle = 0
  LockPosition = false
  MeasureType = 1
  OverTolerance = 0.05
  References2D = -> [ComplexSection]
  Rotation = 0
  ScaleType = 0
  TheoreticalExact = false
  Type = 1
  UnderTolerance = -0.05
  X = 57.016
  Y = -2.5
FEATURE [TechDraw::DrawViewBalloon] Balloon028
  BubbleShape = 6
  EndType = 6
  EndTypeScale = 1
  KinkLength = 0
  LockPosition = false
  OriginX = 50.3137
  OriginY = -16.4664
  Rotation = 0
  ScaleType = 0
  ShapeScale = 1
  SourceView = -> Dimension015
  Text = ⌖|⌀0,15|A|B|C
  TextWrapLen = -1
  X = 67.9947
  Y = -13.386
FEATURE [TechDraw::DrawViewBalloon] Balloon031
  BubbleShape = 1
  EndType = 7
  EndTypeScale = 1
  KinkLength = 0
  LockPosition = false
  OriginX = 1.21699
  OriginY = -70.4143
  Rotation = 0
  ScaleType = 0
  ShapeScale = 1
  Text = 4x 2,1×38,1
  TextWrapLen = -1
  X = 364.547
  Y = 230.43
FEATURE [TechDraw::DrawViewDimension] Dimension016
  AngleOverride = false
  Arbitrary = false
  ArbitraryTolerances = false
  EqualTolerance = false
  ExtensionAngle = 0
  FormatSpec = %.2w
  FormatSpecOverTolerance = %+.2w
  FormatSpecUnderTolerance = %+.2w
  Inverted = false
  LineAngle = 0
  LockPosition = false
  MeasureType = 1
  OverTolerance = 0
  References2D = -> [View006]
  Rotation = 0
  ScaleType = 0
  TheoreticalExact = false
  Type = 1
  UnderTolerance = -0.2
  X = -0.783304
  Y = 67.3349
FEATURE [TechDraw::DrawViewDimension] Dimension017
  AngleOverride = false
  Arbitrary = false
  ArbitraryTolerances = false
  EqualTolerance = false
  ExtensionAngle = 0
  FormatSpec = %.2w
  FormatSpecOverTolerance = %+.2w
  FormatSpecUnderTolerance = %+.2w
  Inverted = false
  LineAngle = 0
  LockPosition = false
  MeasureType = 1
  OverTolerance = 0
  References2D = -> [View004]
  Rotation = 0
  ScaleType = 0
  TheoreticalExact = false
  Type = 2
  UnderTolerance = -0.2
  X = 66.4854
  Y = 3.83037
FEATURE [TechDraw::DrawViewBalloon] Balloon
  BubbleShape = 6
  EndType = 6
  EndTypeScale = 1
  KinkLength = -0.1
  LockPosition = false
  OriginX = -52.2671
  OriginY = 60.276
  Rotation = 0
  ScaleType = 0
  ShapeScale = 1
  SourceView = -> Dimension016
  Text = B
  TextWrapLen = -1
  X = -63.7256
  Y = 60.3167
FEATURE [TechDraw::DrawViewBalloon] Balloon032
  BubbleShape = 6
  EndType = 6
  EndTypeScale = 1
  KinkLength = 0
  LockPosition = false
  OriginX = 74.9267
  OriginY = 52.2331
  Rotation = 0
  ScaleType = 0
  ShapeScale = 1
  SourceView = -> Dimension017
  Text = C
  TextWrapLen = -1
  X = 74.8644
  Y = 64.3015
FEATURE [TechDraw::DrawViewPart] View
  CoarseView = false
  Direction = (0.57735,0.57735,0.57735)
  Focus = 100
  HardHidden = true
  IsoCount = 0
  IsoHidden = false
  IsoVisible = false
  LockPosition = false
  Perspective = false
  Rotation = 0
  Scale = 0.5
  ScaleType = 2
  ScrubCount = 0
  SeamHidden = false
  SeamVisible = true
  SmoothHidden = false
  SmoothVisible = true
  Source = -> [Body003]
  X = 382.139
  XDirection = (0.707107,0,-0.707107)
  Y = 132.114
FEATURE [TechDraw::DrawHatch] Hatch002  label="Hatch002F1"
  HatchPattern = C:/Program Files/FreeCAD 0.21/data/Mod/TechDraw/Patterns/solid.svg
  Source = -> View [Face1]
FEATURE [TechDraw::DrawViewBalloon] Balloon033
  BubbleShape = 1
  EndType = 3
  EndTypeScale = 1
  KinkLength = -0.1
  LockPosition = false
  OriginX = 14.7896
  OriginY = -1.6201
  Rotation = 0
  ScaleType = 0
  ShapeScale = 1
  SourceView = -> View
  TextWrapLen = -1
  X = -105.97
  Y = -73.8417
FEATURE [TechDraw::DrawViewAnnotation] Annotation001
  Font = osifont
  LineSpace = 100
  LockPosition = false
  MaxWidth = -1
  Rotation = 0
  ScaleType = 0
  Text = 10:1
  TextSize = 4
  TextStyle = 0
  X = 85.2815
  Y = 52.8062
FEATURE [TechDraw::DrawViewAnnotation] Annotation
  Font = osifont
  LineSpace = 100
  LockPosition = false
  MaxWidth = -1
  Rotation = 0
  ScaleType = 0
  Text = 1:2
  TextSize = 4
  TextStyle = 0
  X = 377.592
  Y = 102.608
FEATURE [TechDraw::DrawViewAnnotation] Annotation002
  Font = osifont
  LineSpace = 100
  LockPosition = false
  MaxWidth = -1
  Rotation = 0
  ScaleType = 0
  Text = The mid of the datum plane A is preferred to be near | to the lower limit of the flatness tolerance zone. | It can be achieved with an additional bending step. | Aesthetical surfaces colored red on the view | No scratches, burrs or any kind of damage allowed! | Functional surfaces colored blue on the view (all which perpendicular to the aesthetical) | No burrs or other protruding material allowed!
  TextSize = 3
  TextStyle = 0
  X = 296.211
  Y = 100.987
FEATURE [TechDraw::DrawViewBalloon] Balloon034
  BubbleShape = 2
  EndType = 6
  EndTypeScale = 1
  KinkLength = 0
  LockPosition = false
  OriginX = -32.0659
  OriginY = -67.4109
  Rotation = 0
  ScaleType = 0
  ShapeScale = 1
  SourceView = -> Balloon031
  Text = 4
  TextWrapLen = -1
  X = 382.723
  Y = 205.069
FEATURE [TechDraw::DrawViewBalloon] Balloon035
  BubbleShape = 2
  EndType = 6
  EndTypeScale = 1
  KinkLength = 0
  LockPosition = false
  OriginX = -8.22219
  OriginY = -62.5538
  Rotation = 0
  ScaleType = 0
  ShapeScale = 1
  SourceView = -> Dimension
  Text = 4
  TextWrapLen = -1
  X = 11.1048
  Y = -62.8042
FEATURE [TechDraw::DrawViewBalloon] Balloon036
  BubbleShape = 2
  EndType = 6
  EndTypeScale = 1
  KinkLength = 0
  LockPosition = false
  OriginX = -98.0336
  OriginY = -1.14343
  Rotation = 0
  ScaleType = 0
  ShapeScale = 1
  SourceView = -> Annotation002
  Text = 4
  TextWrapLen = -1
  X = -88.9284
  Y = -4.18168
FEATURE [TechDraw::DrawViewBalloon] Balloon037
  BubbleShape = 6
  EndType = 0
  EndTypeScale = 1
  KinkLength = 7
  LockPosition = false
  OriginX = 41.055
  OriginY = 0.028369
  Rotation = 0
  ScaleType = 0
  ShapeScale = 1
  SourceView = -> View006
  Text = ⌓|0,2|A|B|C
  TextWrapLen = -1
  X = 89.9763
  Y = 13.2095
FEATURE [TechDraw::DrawViewDimension] Dimension019
  AngleOverride = false
  Arbitrary = false
  ArbitraryTolerances = false
  EqualTolerance = true
  ExtensionAngle = 0
  FormatSpec = 4× 2×R%.2w
  FormatSpecOverTolerance = %+.2w
  FormatSpecUnderTolerance = %+.2w
  Inverted = false
  LineAngle = 0
  LockPosition = false
  MeasureType = 1
  OverTolerance = 0
  References2D = -> [View006]
  Rotation = 0
  ScaleType = 0
  TheoreticalExact = false
  Type = 4
  UnderTolerance = 0
  X = 73.366
  Y = 2.54261
FEATURE [TechDraw::DrawViewBalloon] Balloon038
  BubbleShape = 1
  EndType = 0
  EndTypeScale = 1
  KinkLength = 0
  LockPosition = false
  OriginX = 0.621503
  OriginY = -45.8906
  Rotation = 0
  ScaleType = 0
  ShapeScale = 1
  SourceView = -> View005
  TextWrapLen = -1
  X = 30.0528
  Y = -79.7274
FEATURE [TechDraw::DrawViewBalloon] Balloon039
  BubbleShape = 6
  EndType = 0
  EndTypeScale = 1
  KinkLength = -0.1
  LockPosition = false
  OriginX = 0.5
  OriginY = 0.0360529
  Rotation = 0
  ScaleType = 0
  ShapeScale = 1
  SourceView = -> View005
  Text = ⏥|0,2
  TextWrapLen = -1
  X = 23.2193
  Y = -0.045215
FEATURE [TechDraw::DrawViewBalloon] Balloon040
  BubbleShape = 6
  EndType = 6
  EndTypeScale = 1
  KinkLength = -0.1
  LockPosition = false
  OriginX = 0.524374
  OriginY = 42.8391
  Rotation = 0
  ScaleType = 0
  ShapeScale = 1
  SourceView = -> View005
  Text = A
  TextWrapLen = -1
  X = 16.7415
  Y = 42.6636
FEATURE [TechDraw::DrawPage] Page  label="PBF4_Drawing"
  KeepUpdated = true
  NextBalloonIndex = 57
  ProjectionType = 0
  Template = -> Template
  Views = -> [View004,View005,View006,Balloon021,Dimension,Dimension011,Balloon025,Balloon026,Balloon027,ComplexSection,Dimension012,Dimension013,Dimension014,Dimension015,Balloon028,Balloon031,Dimension016,Dimension017,Balloon,Balloon032,View,Balloon033,Annotation001,Annotation,Annotation002,Balloon034,Balloon035,Balloon036,Balloon037,Dimension019,Balloon038,Balloon039,Balloon040]
FEATURE [TechDraw::DrawSVGTemplate] Template001
  Height = 210
  Orientation = 1
  Template = C:/Program Files/FreeCAD 0.21/data/Mod/TechDraw/Templates/A4_Landscape_blank.svg
  Width = 297
FEATURE [TechDraw::DrawViewPart] View007
  CoarseView = false
  Direction = (0,0,1)
  Focus = 100
  HardHidden = false
  IsoCount = 0
  IsoHidden = false
  IsoVisible = true
  LockPosition = false
  Perspective = false
  Rotation = 0
  ScaleType = 0
  ScrubCount = 0
  SeamHidden = false
  SeamVisible = true
  SmoothHidden = false
  SmoothVisible = true
  Source = -> [Body003]
  X = 148.5
  XDirection = (1,0,0)
  Y = 105
FEATURE [TechDraw::DrawPage] Page001  label="PBF4_dxf"
  KeepUpdated = true
  NextBalloonIndex = 1
  ProjectionType = 0
  Template = -> Template001
  Views = -> [View007]
FEATURE [TechDraw::DrawHatch] Hatch007  label="Hatch007F3"
  HatchPattern = C:/Program Files/FreeCAD 0.21/data/Mod/TechDraw/Patterns/solid.svg
  Source = -> View [Face3,Face92,Face2,Face59,Face56,Face58,Face57]
FEATURE [TechDraw::DrawHatch] Hatch008  label="Hatch008F32"
  HatchPattern = C:/Program Files/FreeCAD 0.21/data/Mod/TechDraw/Patterns/solid.svg
  Source = -> View [Face32,Face37,Face34,Face33,Face69,Face68,Face65,Face61,Face87,Face29,Face86,Face30,Face84,Face31,Face85,Face28]
FEATURE [TechDraw::DrawHatch] Hatch009  label="Hatch009F64"
  HatchPattern = C:/Program Files/FreeCAD 0.21/data/Mod/TechDraw/Patterns/solid.svg
  Source = -> View [Face64,Face66,Face62,Face63,Face36,Face35,Face70,Face71,Face67,Face39,Face60,Face38]
